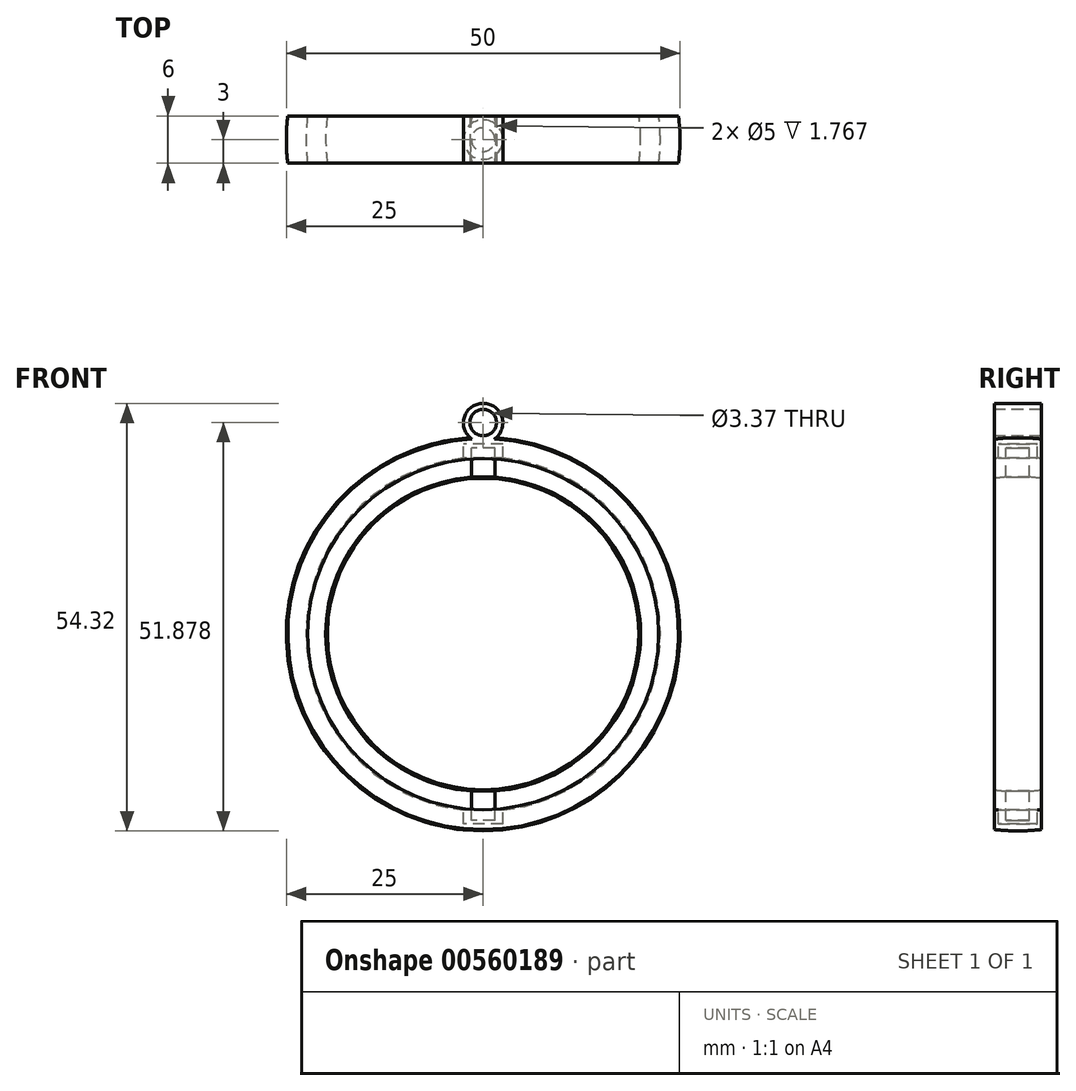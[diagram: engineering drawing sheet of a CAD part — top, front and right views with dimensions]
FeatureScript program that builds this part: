
annotation { "Feature Type Name" : "Feature", "Feature Type Description" : "" }
export const myFeature = defineFeature(function(context is Context, id is Id, definition is map)
    precondition{}
    {
        {
            var Q0;
            Q0=qCreatedBy(makeId("Front.planeOp"),FACE);
            var sketch = newSketch(context, id + "F0", { "sketchPlane" : qUnion([Q0])});
            skCircle(sketch, "E0", {"center": v(0, 0) * mm, "radius": 25 * mm});
            skCircle(sketch, "E1", {"center": v(0, 0) * mm, "radius": 22.5 * mm});
            skCircle(sketch, "E2", {"center": v(0, 0) * mm, "radius": 20 * mm});
            skLineSegment(sketch, "E3.bottom", {"start": v(1.5, -23.64) * mm, "end": v(-1.5, -23.64) * mm});
            skLineSegment(sketch, "E3.top", {"start": v(1.5, 23.64) * mm, "end": v(-1.5, 23.64) * mm});
            skLineSegment(sketch, "E3.left", {"start": v(1.5, -23.64) * mm, "end": v(1.5, 23.64) * mm});
            skLineSegment(sketch, "E3.right", {"start": v(-1.5, -23.64) * mm, "end": v(-1.5, 23.64) * mm});
            skLineSegment(sketch, "E4.bottom", {"start": v(2.5, -24.13) * mm, "end": v(-2.5, -24.13) * mm});
            skLineSegment(sketch, "E4.top", {"start": v(2.5, 24.13) * mm, "end": v(-2.5, 24.13) * mm});
            skLineSegment(sketch, "E4.left", {"start": v(2.5, -24.13) * mm, "end": v(2.5, 24.13) * mm});
            skLineSegment(sketch, "E4.right", {"start": v(-2.5, -24.13) * mm, "end": v(-2.5, 24.13) * mm});
            skSolve(sketch);
        }
        {
            var Q0;
            Q0=qCreatedBy(makeId("Front.planeOp"),FACE);
            var sketch = newSketch(context, id + "F1", { "sketchPlane" : qUnion([Q0])});
            skCircle(sketch, "E5.0", {"center": v(0, 0) * mm, "radius": 25 * mm});
            skArc(sketch, "E5.1", {"start": v(-2.5, 22.36) * mm, "mid": v(-22.5, 0) * mm, "end": v(-2.5, -22.36) * mm});
            skArc(sketch, "E5.2", {"start": v(-1.5, 19.94) * mm, "mid": v(-20, 0) * mm, "end": v(-1.5, -19.94) * mm});
            skLineSegment(sketch, "E5.3", {"start": v(1.5, -23.64) * mm, "end": v(-1.5, -23.64) * mm});
            skLineSegment(sketch, "E5.4", {"start": v(1.5, 23.64) * mm, "end": v(-1.5, 23.64) * mm});
            skLineSegment(sketch, "E5.5", {"start": v(1.5, -23.64) * mm, "end": v(1.5, -19.94) * mm});
            skLineSegment(sketch, "E5.6", {"start": v(-1.5, -23.64) * mm, "end": v(-1.5, -19.94) * mm});
            skPoint(sketch, "E5.7", {"position": v(0, 0) * mm});
            skLineSegment(sketch, "E5.8", {"start": v(2.5, -24.13) * mm, "end": v(-2.5, -24.13) * mm});
            skLineSegment(sketch, "E5.9", {"start": v(2.5, 24.13) * mm, "end": v(-2.5, 24.13) * mm});
            skLineSegment(sketch, "E5.10", {"start": v(2.5, -24.13) * mm, "end": v(2.5, -22.36) * mm});
            skLineSegment(sketch, "E5.11", {"start": v(-2.5, -24.13) * mm, "end": v(-2.5, -22.36) * mm});
            skPoint(sketch, "E5.12", {"position": v(0, 0) * mm});
            skLineSegment(sketch, "E6.trimOffspring", {"start": v(-2.5, 22.36) * mm, "end": v(-2.5, 24.13) * mm});
            skLineSegment(sketch, "E7.trimOffspring", {"start": v(2.5, 22.36) * mm, "end": v(2.5, 24.13) * mm});
            skLineSegment(sketch, "E8.trimOffspring", {"start": v(-1.5, 19.94) * mm, "end": v(-1.5, 23.64) * mm});
            skLineSegment(sketch, "E9.trimOffspring", {"start": v(1.5, 19.94) * mm, "end": v(1.5, 23.64) * mm});
            skArc(sketch, "E10.trimOffspring", {"start": v(2.5, -22.36) * mm, "mid": v(22.5, 0) * mm, "end": v(2.5, 22.36) * mm});
            skArc(sketch, "E11.trimOffspring", {"start": v(1.5, -19.94) * mm, "mid": v(20, 0) * mm, "end": v(1.5, 19.94) * mm});
            skSolve(sketch);
        }
        {
            var Q0;
            Q0=qCreatedBy(makeId("Front.planeOp"),FACE);
            var sketch = newSketch(context, id + "F2", { "sketchPlane" : qUnion([Q0])});
            skCircle(sketch, "E12.0", {"center": v(0, 0) * mm, "radius": 25 * mm});
            skArc(sketch, "E12.1", {"start": v(-2.5, 22.36) * mm, "mid": v(-22.5, 0) * mm, "end": v(-2.5, -22.36) * mm});
            skArc(sketch, "E12.2", {"start": v(-1.5, 19.94) * mm, "mid": v(-20, 0) * mm, "end": v(-1.5, -19.94) * mm});
            skLineSegment(sketch, "E12.3", {"start": v(1.5, -23.64) * mm, "end": v(-1.5, -23.64) * mm});
            skLineSegment(sketch, "E12.4", {"start": v(1.5, 23.64) * mm, "end": v(-1.5, 23.64) * mm});
            skLineSegment(sketch, "E12.5", {"start": v(1.5, -23.64) * mm, "end": v(1.5, -19.94) * mm});
            skLineSegment(sketch, "E12.6", {"start": v(-1.5, -23.64) * mm, "end": v(-1.5, -19.94) * mm});
            skPoint(sketch, "E12.7", {"position": v(0, 0) * mm});
            skLineSegment(sketch, "E12.8", {"start": v(2.5, -24.13) * mm, "end": v(-2.5, -24.13) * mm});
            skLineSegment(sketch, "E12.9", {"start": v(2.5, 24.13) * mm, "end": v(-2.5, 24.13) * mm});
            skLineSegment(sketch, "E12.10", {"start": v(2.5, -24.13) * mm, "end": v(2.5, -22.36) * mm});
            skLineSegment(sketch, "E12.11", {"start": v(-2.5, -24.13) * mm, "end": v(-2.5, -22.36) * mm});
            skPoint(sketch, "E12.12", {"position": v(0, 0) * mm});
            skLineSegment(sketch, "E12.13", {"start": v(-2.5, 22.36) * mm, "end": v(-2.5, 24.13) * mm});
            skLineSegment(sketch, "E12.14", {"start": v(2.5, 22.36) * mm, "end": v(2.5, 24.13) * mm});
            skLineSegment(sketch, "E12.15", {"start": v(-1.5, 19.94) * mm, "end": v(-1.5, 23.64) * mm});
            skLineSegment(sketch, "E12.16", {"start": v(1.5, 19.94) * mm, "end": v(1.5, 23.64) * mm});
            skArc(sketch, "E12.17", {"start": v(2.5, -22.36) * mm, "mid": v(22.5, 0) * mm, "end": v(2.5, 22.36) * mm});
            skArc(sketch, "E12.18", {"start": v(1.5, -19.94) * mm, "mid": v(20, 0) * mm, "end": v(1.5, 19.94) * mm});
            skLineSegment(sketch, "E13", {"start": v(0, 25.22) * mm, "end": v(0, -25.23) * mm});
            skSolve(sketch);
        }
        {
            var Q0;
            Q0=qCreatedBy(makeId("Front.planeOp"),FACE);
            var sketch = newSketch(context, id + "F3", { "sketchPlane" : qUnion([Q0])});
            skArc(sketch, "E14.0", {"start": v(0, -25) * mm, "mid": v(25, 0) * mm, "end": v(0, 25) * mm});
            skLineSegment(sketch, "E14.3", {"start": v(1.5, -23.64) * mm, "end": v(0, -23.64) * mm});
            skLineSegment(sketch, "E14.4", {"start": v(1.5, 23.64) * mm, "end": v(0, 23.64) * mm});
            skLineSegment(sketch, "E14.5", {"start": v(1.5, -23.64) * mm, "end": v(1.5, -19.94) * mm});
            skPoint(sketch, "E14.7", {"position": v(0, 0) * mm});
            skLineSegment(sketch, "E14.8", {"start": v(2.5, -24.13) * mm, "end": v(0, -24.13) * mm});
            skLineSegment(sketch, "E14.9", {"start": v(2.5, 24.13) * mm, "end": v(0, 24.13) * mm});
            skLineSegment(sketch, "E14.10", {"start": v(2.5, -24.13) * mm, "end": v(2.5, -22.36) * mm});
            skPoint(sketch, "E14.12", {"position": v(0, 0) * mm});
            skLineSegment(sketch, "E14.14", {"start": v(2.5, 22.36) * mm, "end": v(2.5, 24.13) * mm});
            skLineSegment(sketch, "E14.16", {"start": v(1.5, 19.94) * mm, "end": v(1.5, 23.64) * mm});
            skArc(sketch, "E14.17", {"start": v(2.5, -22.36) * mm, "mid": v(22.5, 0) * mm, "end": v(2.5, 22.36) * mm});
            skArc(sketch, "E14.18", {"start": v(1.5, -19.94) * mm, "mid": v(20, 0) * mm, "end": v(1.5, 19.94) * mm});
            skLineSegment(sketch, "E14.19", {"start": v(0, 25) * mm, "end": v(0, 24.13) * mm});
            skPoint(sketch, "E14.1.end.orphan", {"position": v(-2.5, -22.36) * mm});
            skPoint(sketch, "E14.1.start.orphan", {"position": v(-2.5, 22.36) * mm});
            skPoint(sketch, "E14.2.end.orphan", {"position": v(-1.5, -19.94) * mm});
            skPoint(sketch, "E14.2.start.orphan", {"position": v(-1.5, 19.94) * mm});
            skPoint(sketch, "E14.13.end.orphan", {"position": v(-2.5, 24.13) * mm});
            skPoint(sketch, "E14.13.start.orphan", {"position": v(-2.5, 22.36) * mm});
            skPoint(sketch, "E14.15.end.orphan", {"position": v(-1.5, 23.64) * mm});
            skPoint(sketch, "E14.15.start.orphan", {"position": v(-1.5, 19.94) * mm});
            skLineSegment(sketch, "E15.trimOffspring", {"start": v(0, 23.64) * mm, "end": v(0, -23.64) * mm});
            skPoint(sketch, "E14.11.end.orphan", {"position": v(-2.5, -22.36) * mm});
            skPoint(sketch, "E14.11.start.orphan", {"position": v(-2.5, -24.13) * mm});
            skPoint(sketch, "E14.6.end.orphan", {"position": v(-1.5, -19.94) * mm});
            skPoint(sketch, "E14.6.start.orphan", {"position": v(-1.5, -23.64) * mm});
            skPoint(sketch, "E16.orphan", {"position": v(0, 25.22) * mm});
            skPoint(sketch, "E17.orphan", {"position": v(0, -25.23) * mm});
            skLineSegment(sketch, "E18.trimOffspring", {"start": v(0, -24.13) * mm, "end": v(0, -25) * mm});
            skSolve(sketch);
        }
        {
            var Q0;
            Q0 = qSketchRegion(id + "F3", true);
            var Q1;
            Q1=sQuery(id+"F3.wireOp",EDGE,"E15.trimOffspring");
            revolve(context, id + "F4", {"entities" : qUnion([Q0]), "axis" : qUnion([Q1]), "revolveType" : RevolveType.FULL});
        }
        {
            var Q0;
            Q0=qCreatedBy(makeId("Right.planeOp"),FACE);
            var sketch = newSketch(context, id + "F5", { "sketchPlane" : qUnion([Q0])});
            skLineSegment(sketch, "E19.bottom", {"start": v(-3, -30) * mm, "end": v(-33, -30) * mm});
            skLineSegment(sketch, "E19.top", {"start": v(-3, 30) * mm, "end": v(-33, 30) * mm});
            skLineSegment(sketch, "E19.left", {"start": v(-3, -30) * mm, "end": v(-3, 30) * mm});
            skLineSegment(sketch, "E19.right", {"start": v(-33, -30) * mm, "end": v(-33, 30) * mm});
            skPoint(sketch, "E19.middle", {"position": v(-18, 0) * mm});
            skSolve(sketch);
        }
        {
            var Q0;
            Q0=qCreatedBy(makeId("Right.planeOp"),FACE);
            var sketch = newSketch(context, id + "F6", { "sketchPlane" : qUnion([Q0])});
            skLineSegment(sketch, "E20.0", {"start": v(-3, -30) * mm, "end": v(-33, -30) * mm});
            skLineSegment(sketch, "E20.1", {"start": v(-3, 30) * mm, "end": v(-33, 30) * mm});
            skLineSegment(sketch, "E20.2", {"start": v(-3, -30) * mm, "end": v(-3, 30) * mm});
            skLineSegment(sketch, "E20.3", {"start": v(-33, -30) * mm, "end": v(-33, 30) * mm});
            skPoint(sketch, "E20.4", {"position": v(-18, 0) * mm});
            skLineSegment(sketch, "E21.MirrorCS", {"start": v(33, -30) * mm, "end": v(33, 30) * mm});
            skLineSegment(sketch, "E22.MirrorCS", {"start": v(3, -30) * mm, "end": v(3, 30) * mm});
            skLineSegment(sketch, "E23.MirrorCS", {"start": v(3, 30) * mm, "end": v(33, 30) * mm});
            skLineSegment(sketch, "E24.MirrorCS", {"start": v(3, -30) * mm, "end": v(33, -30) * mm});
            skPoint(sketch, "E25.MirrorP", {"position": v(18, 0) * mm});
            skSolve(sketch);
        }
        {
            var Q0;
            Q0 = qSketchRegion(id + "F6", true);
            extrude(context, id + "F7", {"entities" : qUnion([Q0]), "operationType" : NewBodyOperationType.REMOVE, "endBound" : BoundingType.SYMMETRIC, "oppositeDirection" : true, "depth" : 60 * mm, "offsetDistance" : 25 * mm});
        }
        {
            var Q0;
            Q0=qCreatedBy(makeId("Front.planeOp"),FACE);
            var sketch = newSketch(context, id + "F8", { "sketchPlane" : qUnion([Q0])});
            skCircle(sketch, "E26", {"center": v(0, 26.82) * mm, "radius": 2.5 * mm});
            skSolve(sketch);
        }
        {
            var Q0;
            Q0 = qSketchRegion(id + "F8", true);
            extrude(context, id + "F9", {"entities" : qUnion([Q0]), "operationType" : NewBodyOperationType.ADD, "endBound" : BoundingType.SYMMETRIC, "depth" : 6 * mm, "offsetDistance" : 25 * mm});
        }
        {
            var Q0;
            Q0=qCreatedBy(makeId("Front.planeOp"),FACE);
            var sketch = newSketch(context, id + "F10", { "sketchPlane" : qUnion([Q0])});
            skCircle(sketch, "E27", {"center": v(0, 26.88) * mm, "radius": 1.69 * mm});
            skSolve(sketch);
        }
        {
            var Q0;
            Q0 = qSketchRegion(id + "F10", true);
            extrude(context, id + "F11", {"entities" : qUnion([Q0]), "operationType" : NewBodyOperationType.REMOVE, "endBound" : BoundingType.SYMMETRIC, "oppositeDirection" : true, "depth" : 30 * mm, "offsetDistance" : 25 * mm});
        }
    });
